# Revit family: Thorn VOYAGER Style 115
name_source: partatom
category: Lighting Fixtures
revit_build: Autodesk Revit 2016 (Build: 20150220_1215(x64)
units: mm (PartAtom-declared; Revit-internal decimal feet)

## family parameters
Cut with Voids When Loaded = No
Host = Face
Light Source = Yes
OmniClass Number = 23.80.70.11
OmniClass Title = Luminaries for Internal Lighting
Part Type = Normal
Room Calculation Point = No
Round Connector Dimension = Use Diameter
Shared = No

## types (6) — shared parameters
Apparent Load = 6 VA
Assembly Code = D5020200
Body = Thorn_Metal_White
Color Filter = 16777215
Depth = 37 mm  [stored 0.121391 ft]
Description = Escape sign
Dimming Lamp Color Temperature Shift = <None>
Glass = Thorn_Glass_White
Height = 191 mm  [stored 0.62664 ft]
Lamp = LED
Manufacturer = Thorn Lighting
Photometric Web File = 42180768+22168595_(STD-LEO).IES
Tilt Angle = 180.00°
URL = http://www.thornlighting.com
Voltage = 230 V
Width = 265 mm  [stored 0.869423 ft]
zero-valued in all types: Default Elevation

## per-type parameters (varying)
| type | Escape Bottom | Escape Left & Right | Escape Top | Model | Offset Body | Recessed | Surface Mount |
| Voyager Style MS + Bottom | Yes | No | No | 96222360 | 0 mm  [stored 0 ft] | No | Yes |
| Voyager Style MS FSR + Top | No | No | Yes | 96222360+96222371 | 57 mm  [stored 0.187008 ft] | Yes | No |
| Voyager Style MS + Left/Right | No | Yes | No | 96222360 | 0 mm  [stored 0 ft] | No | Yes |
| Voyager Style MS FSR + Left/Right | No | Yes | No | 96222360+96222371 | 57 mm  [stored 0.187008 ft] | Yes | No |
| Voyager Style MS FSR + Bottom | Yes | No | No | 96222360+96222371 | 57 mm  [stored 0.187008 ft] | Yes | No |
| Voyager Style MS + Top | No | No | Yes | 96222360 | 0 mm  [stored 0 ft] | No | Yes |

note: [stored X ft] marks values corroborated as IEEE doubles in the binary element streams (Revit-internal decimal feet)

## geometry (parser evidence)
native form markers: Sweep x4
no freeform markers — native parametric forms only
